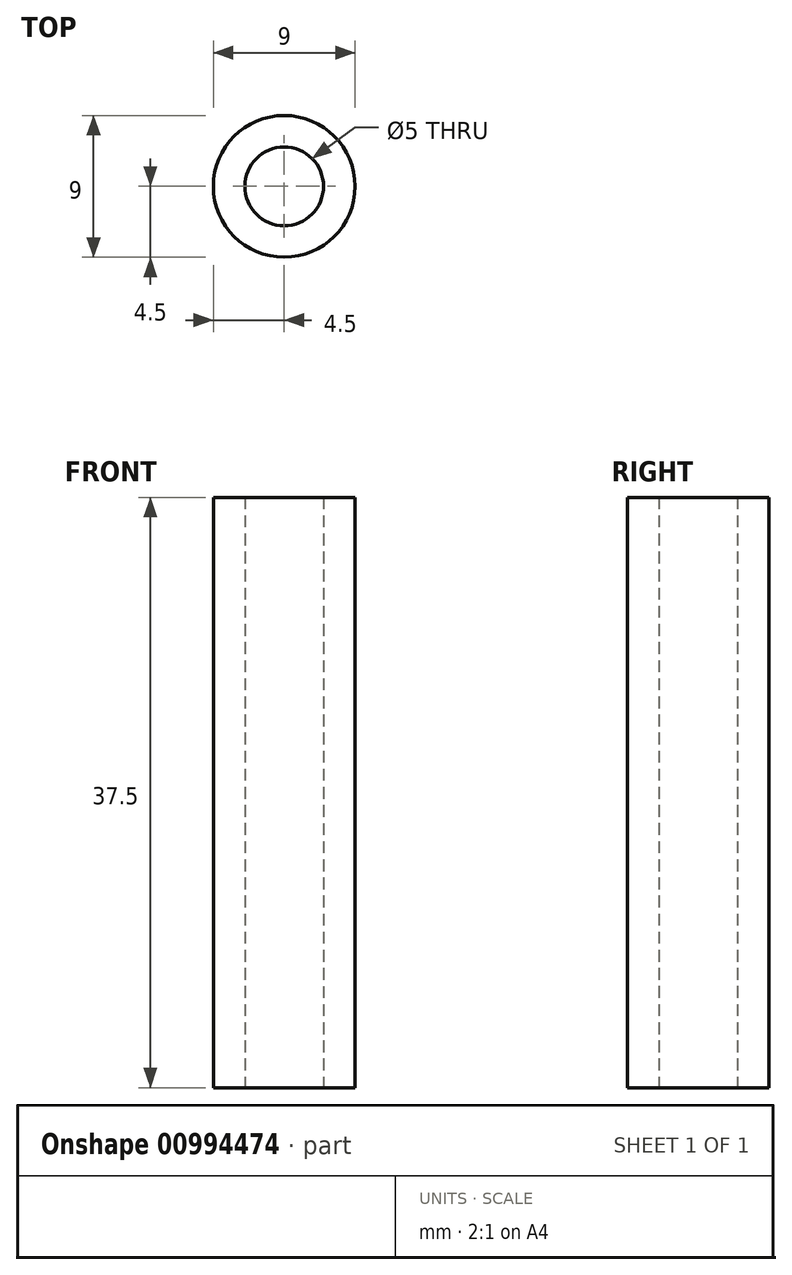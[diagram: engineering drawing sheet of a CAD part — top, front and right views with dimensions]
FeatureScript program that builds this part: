
annotation { "Feature Type Name" : "Feature", "Feature Type Description" : "" }
export const myFeature = defineFeature(function(context is Context, id is Id, definition is map)
    precondition{}
    {
        {
            assignVariable(context, id + "F0", {"name" : "tube_length", "anyValue" : 37.5});
        }
        {
            var Q0;
            Q0=qCreatedBy(makeId("Top.planeOp"),FACE);
            var sketch = newSketch(context, id + "F1", { "sketchPlane" : qUnion([Q0])});
            skCircle(sketch, "E0", {"center": v(0, 0) * mm, "radius": 2.5 * mm});
            skCircle(sketch, "E1", {"center": v(0, 0) * mm, "radius": 4.5 * mm});
            skSolve(sketch);
        }
        {
            var Q0;
            Q0=makeQuery(id+"F1.imprint","IMPRINT",FACE,{"disambiguationData":[TD([[makeQuery(id+"F1.imprint","IMPRINT",EDGE,{"derivedFrom":sQuery(id+"F1.wireOp",EDGE,"E0")}),-1.0]])]});
            extrude(context, id + "F2", {"entities" : qUnion([Q0]), "depth" : (getVariable(context, 'tube_length')) * mm, "offsetDistance" : 25 * mm});
        }
    });
